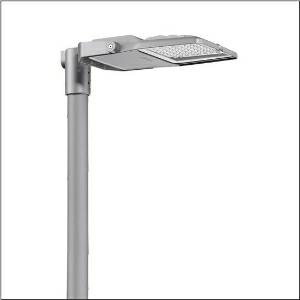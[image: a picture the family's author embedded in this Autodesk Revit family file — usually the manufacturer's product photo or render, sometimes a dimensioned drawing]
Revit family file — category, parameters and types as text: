
# Revit family: floodlight_fl_21_iq_mini___pl64_5xa7771b2e3a_ab64
name_source: partatom
category: Lighting Fixtures
units: mm (PartAtom-declared; Revit-internal decimal feet)

## family parameters
Cut with Voids When Loaded = No
Host = Face
Light Source = No
Part Type = Normal
Room Calculation Point = No
Round Connector Dimension = Use Diameter
Shared = No

## types (1)
- --- (1 x LED, 6020 lm, 45.5 W, 3000K)
    Apparent Load = 46 VA
    CIE Flux Codes = 28 80 98 100 100
    Color Rendering = 70
    Color Temperature = 3000K
    Default Elevation = 1800 mm
    Description = Floodlight FL 21 iQ mini, floodlight, primary light control with lens, of PMMA, primary optical cover: protective disc, of toughened safety glass, transparent, light distribution: PL64, light emission: direct distribution, installation type: surface-mounted, LED, High Power LED, rated luminous flux: 6.020lm, luminous efficacy: 132lm/W, light colour: 730, colour temperature: 3000K, control gear: iQ Comfort/DALI, control: Auto-Match, Temp-Guard, Lumen-Switch, Night-Set, Smart-Wire, Light-Fading, Desk-Remote (wireless, voltage-free reading and setting of iQ features in the workshop via application-optimized NFC function/RFID function), optimised constant luminous flux control (CLO 2.0), with terminal, 6-pole, mains connection: 220..240V, AC, 50/60Hz, start of lifetime: 46W, end of service life: 48W, reduction: 22W, luminaire housing, of diecast aluminium, powder-coated, Siteco® metallic grey (DB 702S), corrosivity category C5 mid according to DIN EN ISO 12944, suitable for swimming pools, chlorine-resistant, sealing non-destructively replaceable, please order mast flange separately, mast bracket, of steel, galvanised, powder-coated, Siteco® metallic grey (DB 702S), protection rating (complete): IP66, insulation class (complete): insulation class II (safety insulation), certification: CE, ENEC, VDE, protection symbol: D, impact resistance: IK08, permissible operating ambient temperature: -40..+40°C, permissible operating ambient temperature for outdoor applications: -40..+50°C, standard: DIN EN 12944, LABS conformity tested according to VDMA 24364:2018-05, packaging unit: 1 piece

Light Distribution: PL64
    Height = 70 mm
    Lamp = 1 x LED
    Lamp Light Flux = 6020 lm
    Lamp Power = 45.5 W
    Lamp count = 1
    Length = 485 mm
    Luminous efficacy = 132 lm/W
    Manufacturer = Siteco
    ModVariant = No
    Model = 5XA7771B2E3A
    Number of Poles = 1
    OnlyDefault = Yes
    Power Factor = 1
    Product Name = Floodlight FL 21 iQ mini | PL64
    Product group = floodlight | pylon annexe
    ProductGroupID = 6200
    Protection Class = Protection class II
    Protection Degree = IP 66
    RLX_Detail_Level = 1
    RLX_Emergency_Light_Flux = 0 lm
    RLX_Emergency_Type = 0
    RLX_Emergency_Type_DB = No
    RlxData = <blob elided: 101233 chars, md5=534d3a96>
    Socket = socket
    Standby Power = 0 W
    System Light Flux = 6020 lm
    System Power = 46 W
    Type Comments = factory setting: luminous flux: 100 % | dim-lin: 254 | 463 mA
    Type Image = l_1007125.jpg
    URL = http://relux.com
    VarID = @adj_167154
    Voltage = 0 V
    Weight = 0.00 kg
    Width = 337 mm

## geometry (parser evidence)
native form markers: Blend x4, Sweep x12
no freeform markers — native parametric forms only
